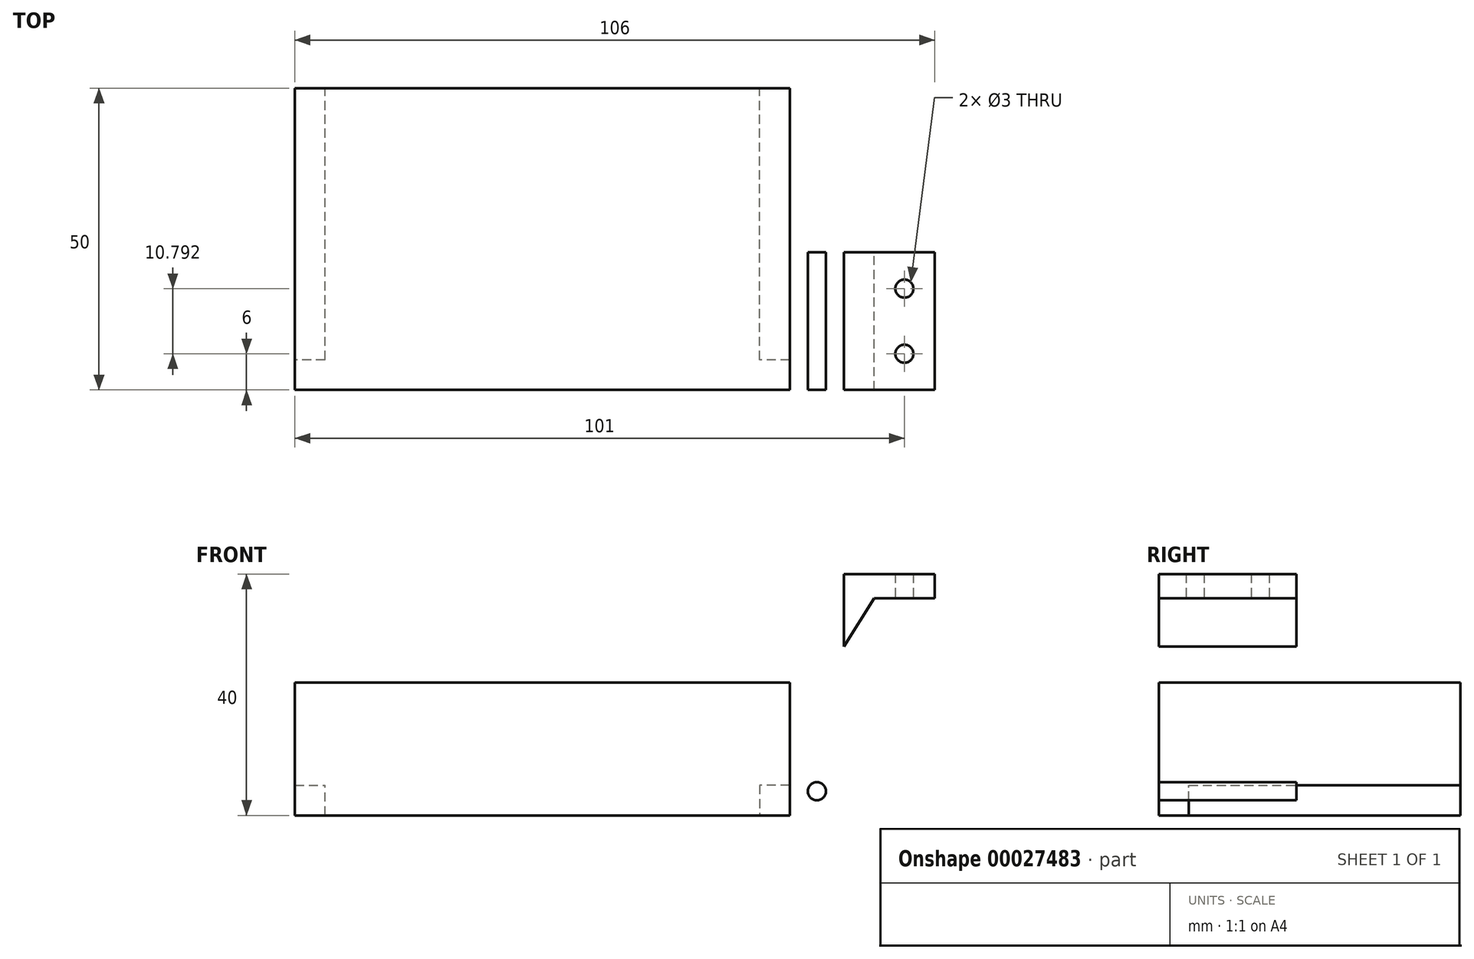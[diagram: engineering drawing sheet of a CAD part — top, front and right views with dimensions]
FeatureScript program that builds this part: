
annotation { "Feature Type Name" : "Feature", "Feature Type Description" : "" }
export const myFeature = defineFeature(function(context is Context, id is Id, definition is map)
    precondition{}
    {
        {
            var Q0;
            Q0=qCreatedBy(makeId("Top.planeOp"),FACE);
            var sketch = newSketch(context, id + "F0", { "sketchPlane" : qUnion([Q0])});
            skLineSegment(sketch, "E0.rect.bottom", {"start": v(50, 25) * mm, "end": v(-50, 25) * mm});
            skLineSegment(sketch, "E0.rect.top", {"start": v(50, -25) * mm, "end": v(-50, -25) * mm});
            skLineSegment(sketch, "E0.rect.left", {"start": v(50, 25) * mm, "end": v(50, -25) * mm});
            skLineSegment(sketch, "E0.rect.right", {"start": v(-50, 25) * mm, "end": v(-50, -25) * mm});
            skPoint(sketch, "E0.rect.middle", {"position": v(0, 0) * mm});
            skSolve(sketch);
        }
        {
            var Q0;
            Q0=makeQuery(id+"F0.imprint","IMPRINT",FACE,{"disambiguationData":[TD([[makeQuery(id+"F0.imprint","IMPRINT",EDGE,{"derivedFrom":sQuery(id+"F0.wireOp",EDGE,"E0.rect.bottom")}),1.0]])]});
            extrude(context, id + "F1", {"entities" : qUnion([Q0]), "depth" : 40 * mm});
        }
        {
            var Q0;
            Q0=makeQuery(id+"F1.opExtrude","SWEPT_FACE",FACE,{"disambiguationData":[OSD([sQuery(id+"F0.wireOp",EDGE,"E0.rect.bottom")])]});
            var sketch = newSketch(context, id + "F2", { "sketchPlane" : qUnion([Q0])});
            skLineSegment(sketch, "E1.bottom", {"start": v(-41, 0) * mm, "end": v(41, 0) * mm});
            skLineSegment(sketch, "E1.top", {"start": v(-41, 22) * mm, "end": v(41, 22) * mm});
            skLineSegment(sketch, "E1.left", {"start": v(-41, 0) * mm, "end": v(-41, 22) * mm});
            skLineSegment(sketch, "E1.right", {"start": v(41, 0) * mm, "end": v(41, 22) * mm});
            skLineSegment(sketch, "E2.bottom", {"start": v(-41, 5) * mm, "end": v(-36, 5) * mm});
            skLineSegment(sketch, "E2.top", {"start": v(-41, 0) * mm, "end": v(-36, 0) * mm});
            skLineSegment(sketch, "E2.left", {"start": v(-41, 5) * mm, "end": v(-41, 0) * mm});
            skLineSegment(sketch, "E2.right", {"start": v(-36, 5) * mm, "end": v(-36, 0) * mm});
            skLineSegment(sketch, "E3.bottom", {"start": v(41, 0) * mm, "end": v(36, 0) * mm});
            skLineSegment(sketch, "E3.top", {"start": v(41, 5) * mm, "end": v(36, 5) * mm});
            skLineSegment(sketch, "E3.left", {"start": v(41, 0) * mm, "end": v(41, 5) * mm});
            skLineSegment(sketch, "E3.right", {"start": v(36, 0) * mm, "end": v(36, 5) * mm});
            skSolve(sketch);
        }
        {
            var Q0;
            Q0=makeQuery(id+"F2.imprint","IMPRINT",FACE,{"disambiguationData":[TD([[makeQuery(id+"F2.imprint","IMPRINT",EDGE,{"derivedFrom":sQuery(id+"F2.wireOp",EDGE,"E1.bottom")}),1.0]])]});
            extrude(context, id + "F3", {"entities" : qUnion([Q0]), "operationType" : NewBodyOperationType.REMOVE, "oppositeDirection" : true, "depth" : 45 * mm});
        }
        {
            var Q0;
            Q0=makeQuery(id+"F2.imprint","IMPRINT",FACE,{"disambiguationData":[TD([[makeQuery(id+"F2.imprint","IMPRINT",EDGE,{"derivedFrom":sQuery(id+"F2.wireOp",EDGE,"E1.top")}),1.0]])]});
            var Q1;
            Q1=makeQuery(id+"F2.imprint","IMPRINT",FACE,{"disambiguationData":[TD([[makeQuery(id+"F2.imprint","IMPRINT",EDGE,{"derivedFrom":sQuery(id+"F2.wireOp",EDGE,"E2.bottom")}),-1.0]])]});
            var Q2;
            Q2=makeQuery(id+"F2.imprint","IMPRINT",FACE,{"disambiguationData":[TD([[makeQuery(id+"F2.imprint","IMPRINT",EDGE,{"derivedFrom":sQuery(id+"F2.wireOp",EDGE,"E3.bottom")}),1.0]])]});
            extrude(context, id + "F4", {"entities" : qUnion([Q0, Q1, Q2]), "operationType" : NewBodyOperationType.REMOVE, "oppositeDirection" : true, "depth" : 27.2 * mm});
        }
        {
            var Q0;
            Q0=makeQuery(id+"F4.boolean.opBoolean","COPY",FACE,{"derivedFrom":makeQuery(id+"F4.opExtrude","CAP_FACE",FACE,{"disambiguationData":[OSD([sQuery(id+"F0.wireOp",EDGE,"E0.rect.bottom"),sQuery(id+"F0.wireOp",EDGE,"E0.rect.left"),sQuery(id+"F0.wireOp",EDGE,"E0.rect.right"),sQuery(id+"F2.wireOp",EDGE,"E1.top"),sQuery(id+"F2.wireOp",EDGE,"E1.left"),sQuery(id+"F2.wireOp",EDGE,"E1.right"),sQuery(id+"F2.wireOp",EDGE,"E2.bottom"),sQuery(id+"F2.wireOp",EDGE,"E2.top"),sQuery(id+"F2.wireOp",EDGE,"E2.right"),sQuery(id+"F2.wireOp",EDGE,"E3.bottom"),sQuery(id+"F2.wireOp",EDGE,"E3.top"),sQuery(id+"F2.wireOp",EDGE,"E3.right")])],"isStart":false})});
            var sketch = newSketch(context, id + "F5", { "sketchPlane" : qUnion([Q0])});
            skCircle(sketch, "E4", {"center": v(45.5, 4) * mm, "radius": 1.5 * mm});
            skPoint(sketch, "E5.center.orphan", {"position": v(-45.5, 6.5) * mm});
            skLineSegment(sketch, "E6", {"start": v(0, 40) * mm, "end": v(0, 0) * mm, "construction": true});
            skCircle(sketch, "E7.MirrorC", {"center": v(-45.5, 4) * mm, "radius": 1.5 * mm});
            skLineSegment(sketch, "E8", {"start": v(50, 0) * mm, "end": v(-50, 0) * mm, "construction": true});
            skCircle(sketch, "E9", {"center": v(45.5, 20) * mm, "radius": 1.5 * mm});
            skCircle(sketch, "E10", {"center": v(-45.5, 20) * mm, "radius": 1.5 * mm});
            skSolve(sketch);
        }
        {
            var Q0;
            Q0=makeQuery(id+"F5.imprint","IMPRINT",FACE,{"disambiguationData":[TD([[makeQuery(id+"F5.imprint","IMPRINT",EDGE,{"derivedFrom":sQuery(id+"F5.wireOp",EDGE,"E4")}),1.0]])]});
            var Q1;
            Q1=makeQuery(id+"F5.imprint","IMPRINT",FACE,{"disambiguationData":[TD([[makeQuery(id+"F5.imprint","IMPRINT",EDGE,{"derivedFrom":sQuery(id+"F5.wireOp",EDGE,"E7.MirrorC")}),-1.0]])]});
            var Q2;
            Q2=makeQuery(id+"F5.imprint","IMPRINT",FACE,{"disambiguationData":[TD([[makeQuery(id+"F5.imprint","IMPRINT",EDGE,{"derivedFrom":sQuery(id+"F5.wireOp",EDGE,"E9")}),1.0]])]});
            var Q3;
            Q3=makeQuery(id+"F5.imprint","IMPRINT",FACE,{"disambiguationData":[TD([[makeQuery(id+"F5.imprint","IMPRINT",EDGE,{"derivedFrom":sQuery(id+"F5.wireOp",EDGE,"E10")}),1.0]])]});
            extrude(context, id + "F6", {"entities" : qUnion([Q0, Q1, Q2, Q3]), "operationType" : NewBodyOperationType.REMOVE, "oppositeDirection" : true, "depth" : 25 * mm});
        }
        {
            var Q0;
            Q0=makeQuery(id+"F4.boolean.opBoolean","COPY",FACE,{"derivedFrom":makeQuery(id+"F4.opExtrude","CAP_FACE",FACE,{"disambiguationData":[OSD([sQuery(id+"F0.wireOp",EDGE,"E0.rect.bottom"),sQuery(id+"F0.wireOp",EDGE,"E0.rect.left"),sQuery(id+"F0.wireOp",EDGE,"E0.rect.right"),sQuery(id+"F2.wireOp",EDGE,"E1.top"),sQuery(id+"F2.wireOp",EDGE,"E1.left"),sQuery(id+"F2.wireOp",EDGE,"E1.right"),sQuery(id+"F2.wireOp",EDGE,"E2.bottom"),sQuery(id+"F2.wireOp",EDGE,"E2.top"),sQuery(id+"F2.wireOp",EDGE,"E2.right"),sQuery(id+"F2.wireOp",EDGE,"E3.bottom"),sQuery(id+"F2.wireOp",EDGE,"E3.top"),sQuery(id+"F2.wireOp",EDGE,"E3.right")])],"isStart":false})});
            var sketch = newSketch(context, id + "F7", { "sketchPlane" : qUnion([Q0])});
            skLineSegment(sketch, "E11.bottom", {"start": v(-50, 40) * mm, "end": v(-65, 40) * mm});
            skLineSegment(sketch, "E11.top", {"start": v(-50, 28) * mm, "end": v(-65, 28) * mm});
            skLineSegment(sketch, "E11.left", {"start": v(-50, 40) * mm, "end": v(-50, 28) * mm});
            skLineSegment(sketch, "E11.right", {"start": v(-65, 40) * mm, "end": v(-65, 28) * mm});
            skLineSegment(sketch, "E12", {"start": v(-50, 28) * mm, "end": v(-55, 36) * mm});
            skLineSegment(sketch, "E13", {"start": v(-55, 36) * mm, "end": v(-65, 36) * mm});
            skLineSegment(sketch, "E14.MirrorCS", {"start": v(50, 28) * mm, "end": v(55, 36) * mm});
            skLineSegment(sketch, "E15.MirrorCS", {"start": v(55, 36) * mm, "end": v(65, 36) * mm});
            skLineSegment(sketch, "E16.MirrorCS", {"start": v(50, 40) * mm, "end": v(65, 40) * mm});
            skLineSegment(sketch, "E17.MirrorCS", {"start": v(65, 40) * mm, "end": v(65, 28) * mm});
            skLineSegment(sketch, "E18.MirrorCS", {"start": v(50, 28) * mm, "end": v(65, 28) * mm});
            skSolve(sketch);
        }
        {
            var Q0;
            {var subQ5=sQuery(id+"F7.wireOp",EDGE,"E14.MirrorCS");Q0=makeQuery(id+"F7.imprint","IMPRINT",FACE,{"disambiguationData":[TD([[makeQuery(id+"F7.imprint","IMPRINT",EDGE,{"derivedFrom":subQ5}),1.0]])]});}
            var Q1;
            {var subQ2=sQuery(id+"F7.wireOp",EDGE,"E11.bottom");Q1=makeQuery(id+"F7.imprint","IMPRINT",FACE,{"disambiguationData":[TD([[makeQuery(id+"F7.imprint","IMPRINT",EDGE,{"derivedFrom":subQ2}),1.0]])]});}
            extrude(context, id + "F8", {"entities" : qUnion([Q0, Q1]), "operationType" : NewBodyOperationType.ADD, "oppositeDirection" : true, "depth" : 22.8 * mm});
        }
        {
            var Q0;
            Q0=makeQuery(id+"F8.opExtrude","SWEPT_FACE",FACE,{"disambiguationData":[OSD([sQuery(id+"F7.wireOp",EDGE,"E13")])]});
            var sketch = newSketch(context, id + "F9", { "sketchPlane" : qUnion([Q0])});
            skCircle(sketch, "E19", {"center": v(60, 19) * mm, "radius": 1.5 * mm});
            skCircle(sketch, "E20", {"center": v(60, 8.2) * mm, "radius": 1.5 * mm});
            skSolve(sketch);
        }
        {
            var Q0;
            Q0=makeQuery(id+"F8.opExtrude","SWEPT_FACE",FACE,{"disambiguationData":[OSD([sQuery(id+"F7.wireOp",EDGE,"E15.MirrorCS")])]});
            var sketch = newSketch(context, id + "F10", { "sketchPlane" : qUnion([Q0])});
            skCircle(sketch, "E21", {"center": v(-60, 8.2) * mm, "radius": 1.5 * mm});
            skCircle(sketch, "E22", {"center": v(-60, 19) * mm, "radius": 1.5 * mm});
            skSolve(sketch);
        }
        {
            var Q0;
            Q0=makeQuery(id+"F10.imprint","IMPRINT",FACE,{"disambiguationData":[TD([[makeQuery(id+"F10.imprint","IMPRINT",EDGE,{"derivedFrom":sQuery(id+"F10.wireOp",EDGE,"E21")}),1.0]])]});
            var Q1;
            Q1=makeQuery(id+"F10.imprint","IMPRINT",FACE,{"disambiguationData":[TD([[makeQuery(id+"F10.imprint","IMPRINT",EDGE,{"derivedFrom":sQuery(id+"F10.wireOp",EDGE,"E22")}),1.0]])]});
            var Q2;
            Q2=makeQuery(id+"F9.imprint","IMPRINT",FACE,{"disambiguationData":[TD([[makeQuery(id+"F9.imprint","IMPRINT",EDGE,{"derivedFrom":sQuery(id+"F9.wireOp",EDGE,"E20")}),1.0]])]});
            var Q3;
            Q3=makeQuery(id+"F9.imprint","IMPRINT",FACE,{"disambiguationData":[TD([[makeQuery(id+"F9.imprint","IMPRINT",EDGE,{"derivedFrom":sQuery(id+"F9.wireOp",EDGE,"E19")}),1.0]])]});
            extrude(context, id + "F11", {"entities" : qUnion([Q0, Q1, Q2, Q3]), "operationType" : NewBodyOperationType.REMOVE, "oppositeDirection" : true, "depth" : 25 * mm});
        }
    });
